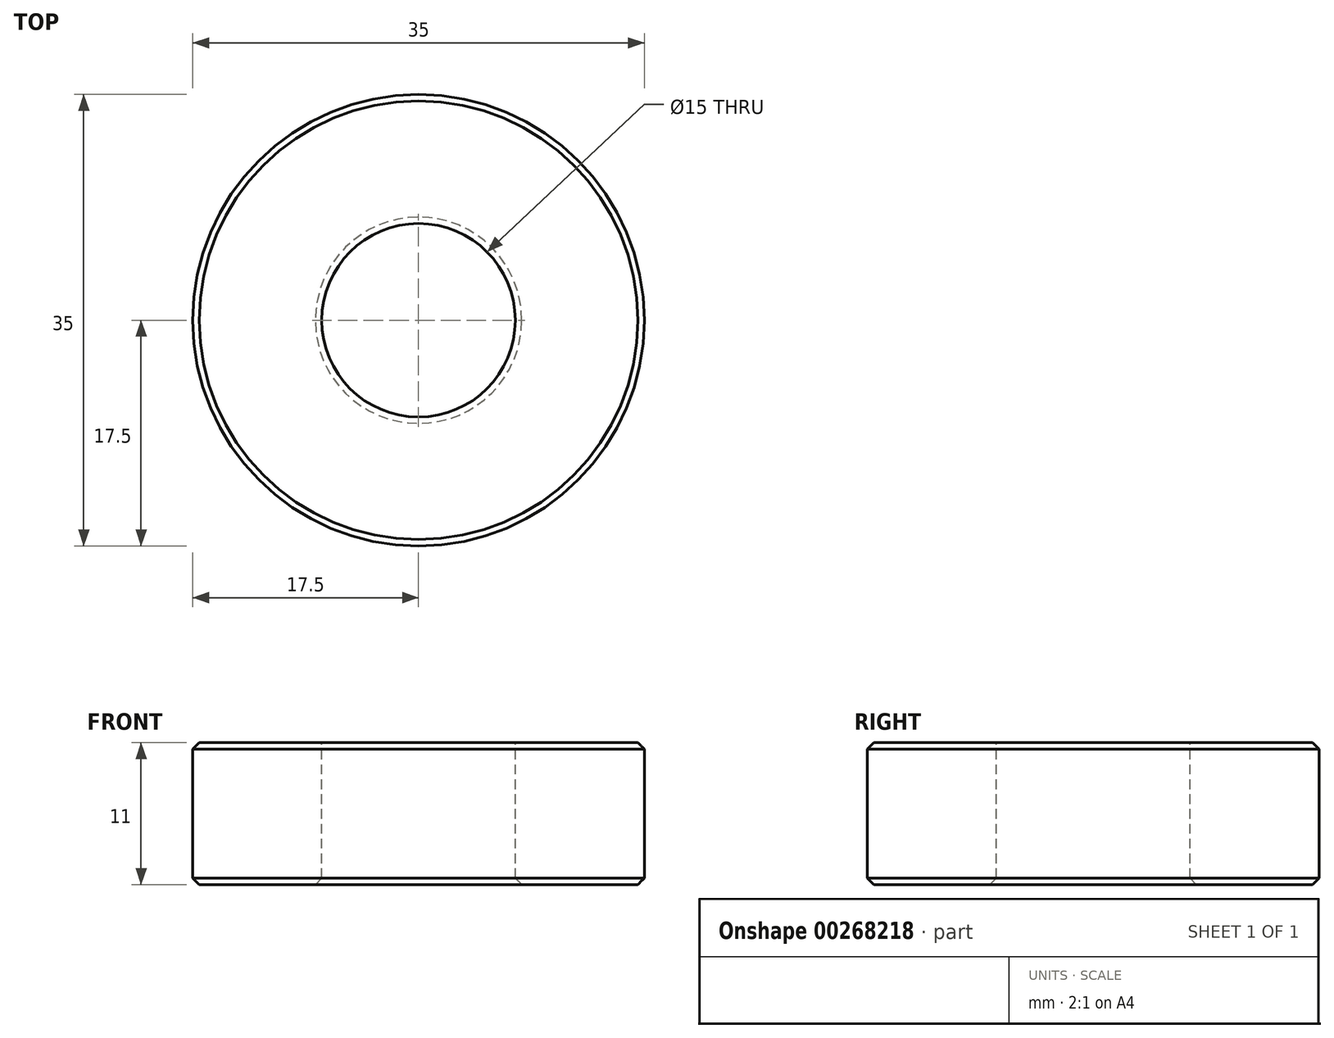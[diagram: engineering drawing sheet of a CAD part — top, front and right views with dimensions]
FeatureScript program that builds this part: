
annotation { "Feature Type Name" : "Feature", "Feature Type Description" : "" }
export const myFeature = defineFeature(function(context is Context, id is Id, definition is map)
    precondition{}
    {
        {
            var Q0;
            Q0=qCreatedBy(makeId("Top.planeOp"),FACE);
            var sketch = newSketch(context, id + "F0", { "sketchPlane" : qUnion([Q0])});
            skCircle(sketch, "E0", {"center": v(0, 0) * mm, "radius": 17.5 * mm});
            skSolve(sketch);
        }
        {
            var Q0;
            Q0 = qSketchRegion(id + "F0", true);
            extrude(context, id + "F1", {"entities" : qUnion([Q0]), "depth" : 11 * mm});
        }
        {
            var Q0;
            Q0=makeQuery(id+"F1.opExtrude","CAP_EDGE",EDGE,{"disambiguationData":[OSD([sQuery(id+"F0.wireOp",EDGE,"E0")])],"isStart":false});
            var Q1;
            Q1=makeQuery(id+"F1.opExtrude","CAP_EDGE",EDGE,{"disambiguationData":[OSD([sQuery(id+"F0.wireOp",EDGE,"E0")])],"isStart":true});
            chamfer(context, id + "F2", {"entities" : qUnion([Q0, Q1]), "width" : 0.5 * mm, "tangentPropagation" : true});
        }
        {
            var Q0;
            Q0=makeQuery(id+"F1.opExtrude","CAP_FACE",FACE,{"disambiguationData":[OSD([sQuery(id+"F0.wireOp",EDGE,"E0")])],"isStart":false});
            var sketch = newSketch(context, id + "F3", { "sketchPlane" : qUnion([Q0])});
            skCircle(sketch, "E1", {"center": v(0, 0) * mm, "radius": 7.5 * mm});
            skSolve(sketch);
        }
        {
            var Q0;
            Q0 = qSketchRegion(id + "F3", true);
            extrude(context, id + "F4", {"entities" : qUnion([Q0]), "operationType" : NewBodyOperationType.REMOVE, "oppositeDirection" : true, "depth" : 40.7 * mm});
        }
        {
            var Q0;
            Q0=makeQuery(id+"F4.boolean.opBoolean","COPY",EDGE,{"derivedFrom":makeQuery(id+"F4.opExtrude","CAP_EDGE",EDGE,{"disambiguationData":[OSD([sQuery(id+"F3.wireOp",EDGE,"E1")])],"isStart":true})});
            var Q1;
            Q1=makeQuery(id+"F4.boolean.opBoolean","INTERSECT",EDGE,{"derivedFrom":[makeQuery(id+"F1.opExtrude","CAP_FACE",FACE,{"disambiguationData":[OSD([sQuery(id+"F0.wireOp",EDGE,"E0")])],"isStart":true}),makeQuery(id+"F4.opExtrude","SWEPT_FACE",FACE,{"disambiguationData":[OSD([sQuery(id+"F3.wireOp",EDGE,"E1")])]})]});
            chamfer(context, id + "F5", {"entities" : qUnion([Q0, Q1]), "width" : 0.5 * mm, "tangentPropagation" : true});
        }
    });
